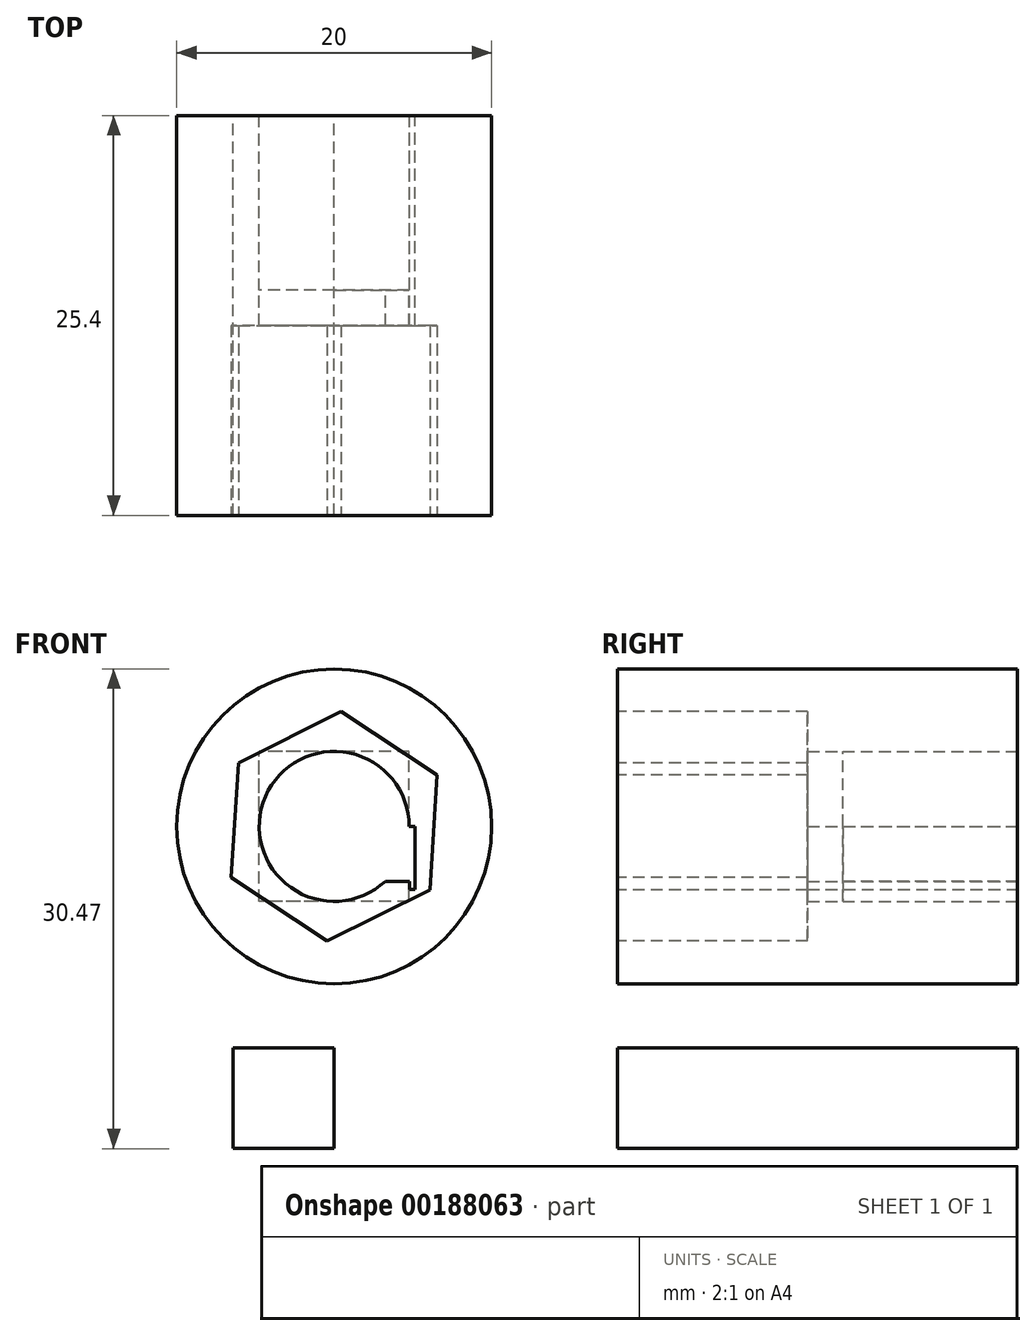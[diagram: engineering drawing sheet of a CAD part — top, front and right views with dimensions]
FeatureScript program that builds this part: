
annotation { "Feature Type Name" : "Feature", "Feature Type Description" : "" }
export const myFeature = defineFeature(function(context is Context, id is Id, definition is map)
    precondition{}
    {
        {
            var Q0;
            Q0=qCreatedBy(makeId("Front.planeOp"),FACE);
            var sketch = newSketch(context, id + "F0", { "sketchPlane" : qUnion([Q0])});
            skCircle(sketch, "E0", {"center": v(0, 0) * mm, "radius": 10 * mm});
            skLineSegment(sketch, "E1.bottom", {"start": v(0, 0) * mm, "end": v(5.14, 0) * mm});
            skLineSegment(sketch, "E1.top", {"start": v(0, -3.48) * mm, "end": v(4.78, -3.48) * mm});
            skLineSegment(sketch, "E1.left", {"start": v(0, 0) * mm, "end": v(0, -3.48) * mm});
            skLineSegment(sketch, "E1.right", {"start": v(5.14, 0) * mm, "end": v(5.14, -3.48) * mm});
            skLineSegment(sketch, "E2.bottom", {"start": v(4.78, -4) * mm, "end": v(5.14, -4) * mm});
            skLineSegment(sketch, "E2.left", {"start": v(4.78, -4) * mm, "end": v(4.78, -3.48) * mm});
            skLineSegment(sketch, "E2.right", {"start": v(5.14, -4) * mm, "end": v(5.14, -3.48) * mm});
            skLineSegment(sketch, "E3.bottom", {"start": v(-6.43, -14.05) * mm, "end": v(0, -14.05) * mm});
            skLineSegment(sketch, "E3.top", {"start": v(-6.43, -20.47) * mm, "end": v(0, -20.47) * mm});
            skLineSegment(sketch, "E3.left", {"start": v(-6.43, -14.05) * mm, "end": v(-6.43, -20.47) * mm});
            skLineSegment(sketch, "E3.right", {"start": v(0, -14.05) * mm, "end": v(0, -20.47) * mm});
            skSolve(sketch);
        }
        {
            var Q0;
            Q0 = qSketchRegion(id + "F0", true);
            extrude(context, id + "F1", {"entities" : qUnion([Q0]), "depth" : 25.4 * mm});
        }
        {
            var Q0;
            Q0=qCreatedBy(makeId("Front.planeOp"),FACE);
            var sketch = newSketch(context, id + "F2", { "sketchPlane" : qUnion([Q0])});
            skLineSegment(sketch, "E4.bottom", {"start": v(4.76, -4.76) * mm, "end": v(-4.76, -4.76) * mm});
            skLineSegment(sketch, "E4.top", {"start": v(4.76, 4.76) * mm, "end": v(-4.76, 4.76) * mm});
            skLineSegment(sketch, "E4.left", {"start": v(4.76, -4.76) * mm, "end": v(4.76, 4.76) * mm});
            skLineSegment(sketch, "E4.right", {"start": v(-4.76, -4.76) * mm, "end": v(-4.76, 4.76) * mm});
            skPoint(sketch, "E4.middle", {"position": v(0, 0) * mm});
            skCircle(sketch, "E5", {"center": v(0, 0) * mm, "radius": 4.76 * mm});
            skSolve(sketch);
        }
        {
            var Q0;
            {var subQ0=sQuery(id+"F2.wireOp",EDGE,"E5");var subQ1=makeQuery(id+"F2.imprint","INTERSECT",VERTEX,{"derivedFrom":[sQuery(id+"F2.wireOp",EDGE,"E4.top"),subQ0]});Q0=makeQuery(id+"F2.imprint","IMPRINT",FACE,{"disambiguationData":[TD([[makeQuery(id+"F2.imprint","IMPRINT",EDGE,{"disambiguationData":[TD([[subQ1,1.0]])],"derivedFrom":subQ0}),1.0]])]});}
            extrude(context, id + "F3", {"entities" : qUnion([Q0]), "operationType" : NewBodyOperationType.REMOVE, "endBound" : BoundingType.THROUGH_ALL, "depth" : 25.4 * mm});
        }
        {
            var Q0;
            Q0 = qSketchRegion(id + "F2", true);
            extrude(context, id + "F4", {"entities" : qUnion([Q0]), "operationType" : NewBodyOperationType.REMOVE, "depth" : 11.1 * mm});
        }
        {
            var Q0;
            Q0=makeQuery(id+"F1.opExtrude","CAP_FACE",FACE,{"disambiguationData":[OSD([sQuery(id+"F0.wireOp",EDGE,"E0")])],"isStart":false});
            var sketch = newSketch(context, id + "F5", { "sketchPlane" : qUnion([Q0])});
            skCircle(sketch, "E6.cCircle", {"center": v(0, 0) * mm, "radius": 6.32 * mm, "construction": true});
            skLineSegment(sketch, "E6.0", {"start": v(0.45, 7.29) * mm, "end": v(6.54, 3.25) * mm});
            skLineSegment(sketch, "E6.1", {"start": v(6.54, 3.25) * mm, "end": v(6.09, -4.04) * mm});
            skLineSegment(sketch, "E6.2", {"start": v(6.09, -4.04) * mm, "end": v(-0.45, -7.29) * mm});
            skLineSegment(sketch, "E6.3", {"start": v(-0.45, -7.29) * mm, "end": v(-6.54, -3.25) * mm});
            skLineSegment(sketch, "E6.4", {"start": v(-6.54, -3.25) * mm, "end": v(-6.09, 4.04) * mm});
            skLineSegment(sketch, "E6.5", {"start": v(-6.09, 4.04) * mm, "end": v(0.45, 7.29) * mm});
            skPoint(sketch, "E6.0.midPoint", {"position": v(3.5, 5.27) * mm});
            skSolve(sketch);
        }
        {
            var Q0;
            Q0 = qSketchRegion(id + "F5", true);
            extrude(context, id + "F6", {"entities" : qUnion([Q0]), "operationType" : NewBodyOperationType.REMOVE, "oppositeDirection" : true, "depth" : 12.06 * mm});
        }
    });
